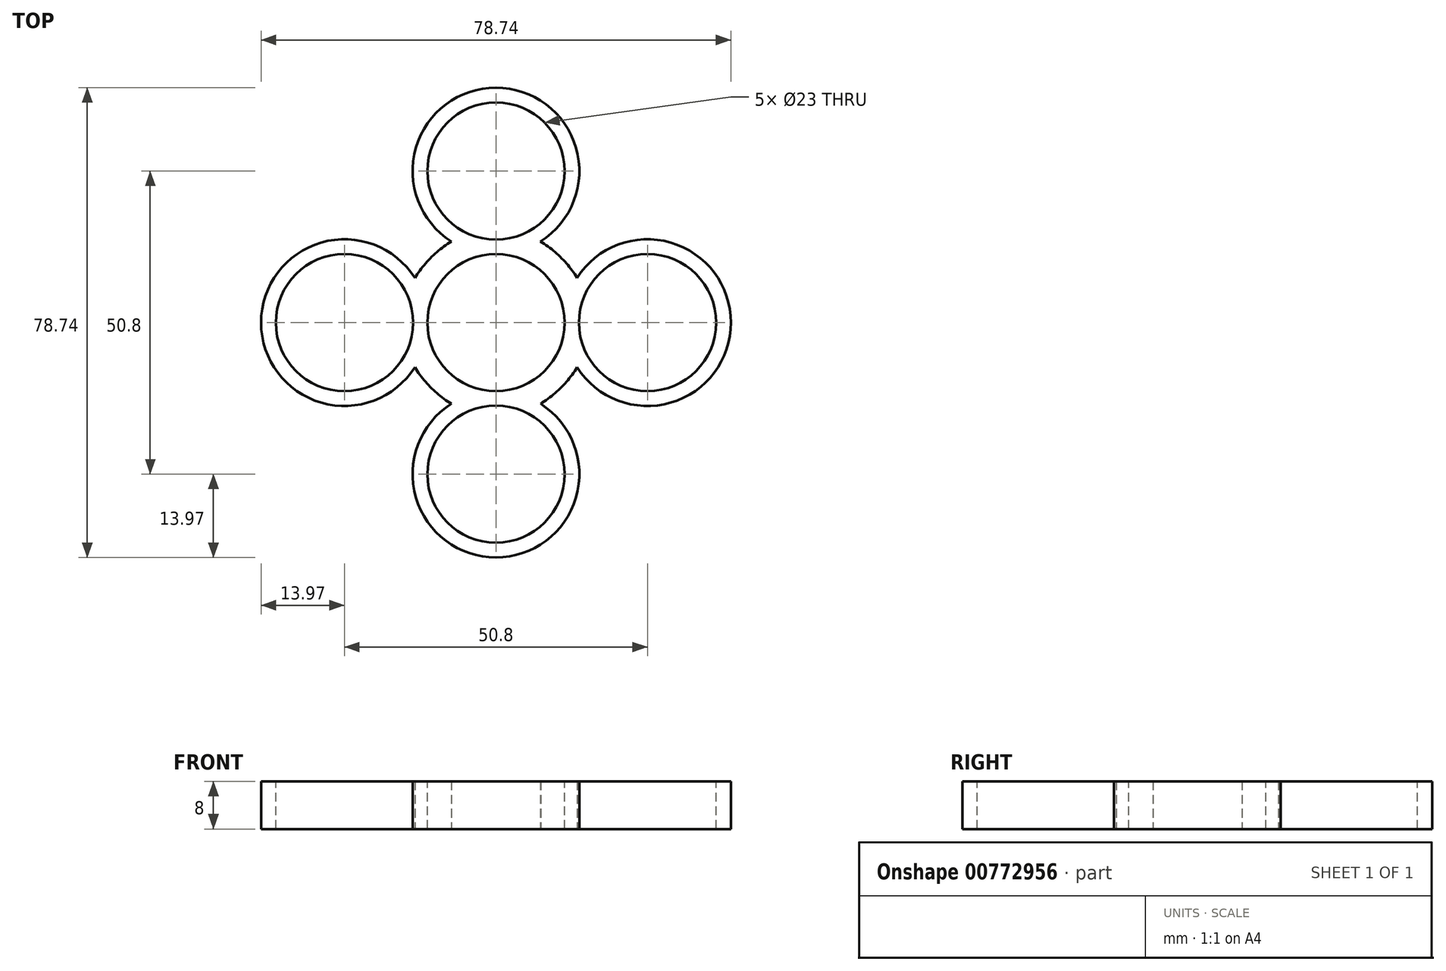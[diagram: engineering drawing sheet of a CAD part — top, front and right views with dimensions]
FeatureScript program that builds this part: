
annotation { "Feature Type Name" : "Feature", "Feature Type Description" : "" }
export const myFeature = defineFeature(function(context is Context, id is Id, definition is map)
    precondition{}
    {
        {
            var Q0;
            Q0=qCreatedBy(makeId("Top.planeOp"),FACE);
            var sketch = newSketch(context, id + "F0", { "sketchPlane" : qUnion([Q0])});
            skCircle(sketch, "E0", {"center": v(0, 0) * mm, "radius": 11.5 * mm});
            skCircle(sketch, "E1", {"center": v(0, -25.4) * mm, "radius": 11.5 * mm});
            skCircle(sketch, "E2", {"center": v(25.4, 0) * mm, "radius": 11.5 * mm});
            skCircle(sketch, "E3", {"center": v(0, 25.4) * mm, "radius": 11.5 * mm});
            skCircle(sketch, "E4", {"center": v(-25.4, 0) * mm, "radius": 11.5 * mm});
            skSolve(sketch);
        }
        {
            var Q0;
            Q0=qCreatedBy(makeId("Top.planeOp"),FACE);
            var sketch = newSketch(context, id + "F1", { "sketchPlane" : qUnion([Q0])});
            skCircle(sketch, "E5", {"center": v(-25.4, 0) * mm, "radius": 13.97 * mm});
            skCircle(sketch, "E6", {"center": v(0, -25.4) * mm, "radius": 13.97 * mm});
            skCircle(sketch, "E7", {"center": v(0, 25.4) * mm, "radius": 13.97 * mm});
            skCircle(sketch, "E8", {"center": v(25.4, 0) * mm, "radius": 13.97 * mm});
            skFitSpline(sketch, "E9", {"points": [v(-15.85, 0) * mm, v(0, 15.84) * mm, v(15.85, 0) * mm, v(0, -15.85) * mm, v(-15.85, 0) * mm]});
            skSolve(sketch);
        }
        {
            var Q0;
            Q0 = qSketchRegion(id + "F1", true);
            extrude(context, id + "F2", {"entities" : qUnion([Q0]), "endBound" : BoundingType.SYMMETRIC, "depth" : 8 * mm, "offsetDistance" : 25.4 * mm});
        }
        {
            var Q0;
            Q0 = qSketchRegion(id + "F0", true);
            extrude(context, id + "F3", {"entities" : qUnion([Q0]), "operationType" : NewBodyOperationType.REMOVE, "endBound" : BoundingType.SYMMETRIC, "oppositeDirection" : true, "depth" : 8 * mm, "offsetDistance" : 25.4 * mm});
        }
    });
